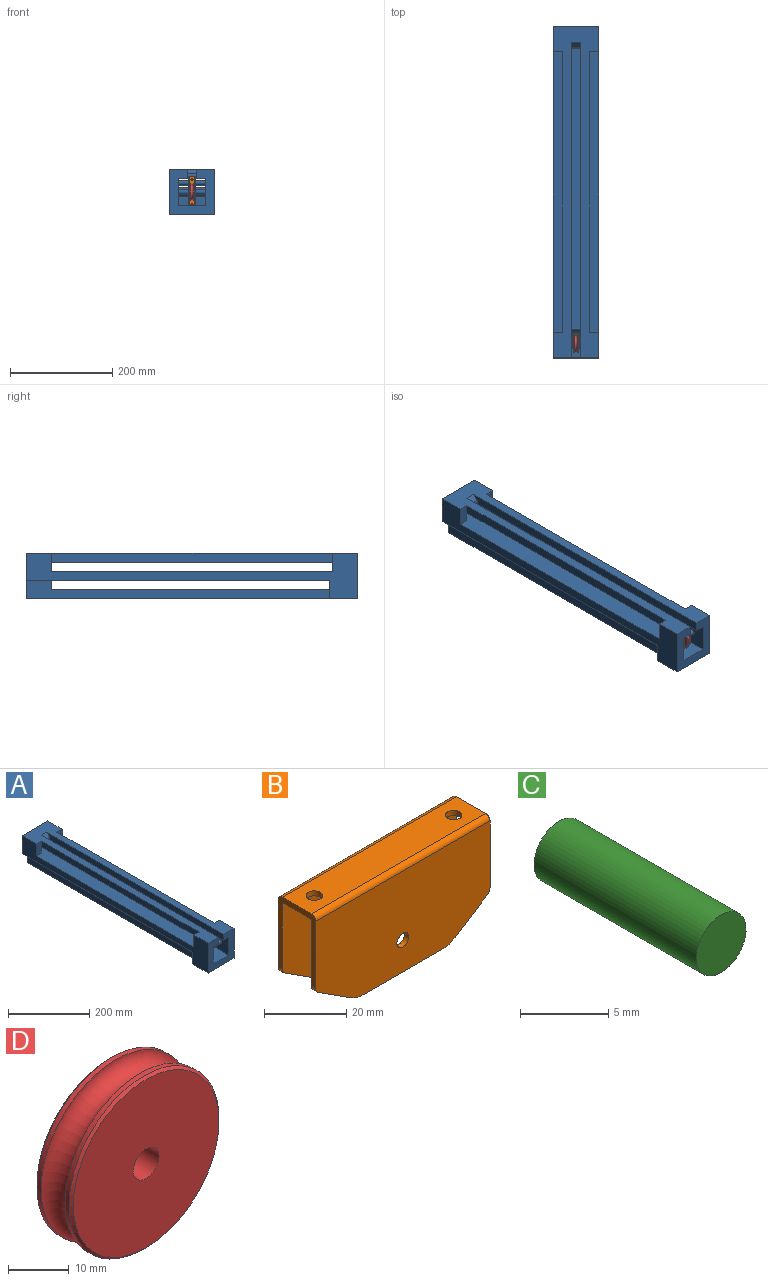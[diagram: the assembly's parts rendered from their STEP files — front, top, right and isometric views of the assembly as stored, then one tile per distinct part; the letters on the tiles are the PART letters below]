
ASSEMBLY  parts=4 mates=3
PART A: 35 faces, bbox 90x650x90 mm
  f0: plane 595x90mm, normal (0,0,-1), area 50850mm2, adj f7,f23,f28,f29,f30,f31,f32,f33
  f1: plane 36x18mm, normal (0,1,0), area 648mm2, adj f4,f9,f16,f22,f34
  f2: cylinder r=5mm len=54mm, axis (-1,0,0), area 1696.5mm2, adj f12,f16
  f3: cylinder r=5mm len=54mm, axis (-1,0,0), area 1696.5mm2, adj f10,f15
  f4: plane 650x90mm, normal (0,0,1), area 27576mm2, adj f1,f5,f7,f8,f9,f11,f13,f14
  f5: plane 90x90mm, normal (0,-1,0), area 4860mm2, adj f4,f6,f12,f16,f17,f18,f26,f27
  f6: plane 650x54mm, normal (0,0,-1), area 24120mm2, adj f5,f7,f8,f9,f10,f12,f15,f16
  f7: plane 90x90mm, normal (0,1,0), area 5832mm2, adj f0,f4,f6,f10,f15,f22,f27,f29
  f8: plane 550x18mm, normal (1,0,0), area 9900mm2, adj f4,f6,f11,f13
  f9: plane 550x18mm, normal (-1,0,0), area 9900mm2, adj f1,f4,f6,f14
  f10: plane 50x18mm, normal (-1,0,0), area 821.5mm2, adj f3,f6,f7,f11,f22
  f11: plane 36x18mm, normal (0,-1,0), area 648mm2, adj f4,f8,f10,f22,f33
  f12: plane 55x54mm, normal (-1,0,0), area 2736.5mm2, adj f2,f5,f6,f13,f21,f22,f23,f24
  f13: plane 36x18mm, normal (0,1,0), area 648mm2, adj f4,f8,f12,f22,f33
  f14: plane 36x18mm, normal (0,-1,0), area 648mm2, adj f4,f9,f15,f22,f34
  f15: plane 50x18mm, normal (1,0,0), area 821.5mm2, adj f3,f6,f7,f14,f22
  f16: plane 55x54mm, normal (1,0,0), area 2736.5mm2, adj f1,f2,f5,f6,f21,f22,f23,f24
  f17: plane 618x18mm, normal (1,0,0), area 10989.9mm2, adj f4,f5,f6,f19,f20,f25
  f18: plane 618x18mm, normal (-1,0,0), area 10989.9mm2, adj f4,f5,f6,f19,f20,f25
  f19: plane 18x9.75mm, normal (0,-0.71,0.71), area 248.1mm2, adj f4,f17,f18,f25
  f20: plane 18x0.61mm, normal (0,-0.48,-0.88), area 12.5mm2, adj f6,f17,f18,f25
  f21: plane 54x8mm, normal (0,-1,0), area 432mm2, adj f12,f16,f23,f24
  f22: plane 600x90mm, normal (0,0,1), area 51930mm2, adj f1,f7,f10,f11,f12,f13,f14,f15
  f23: plane 54x5mm, normal (0,-0.71,-0.71), area 381.8mm2, adj f0,f12,f16,f21
  f24: plane 54x5mm, normal (0,-0.71,0.71), area 381.8mm2, adj f12,f16,f21,f22
  f25: cylinder r=5mm len=18mm, axis (1,0,0), area 167mm2, adj f17,f18,f19,f20
  f26: plane 600x54mm, normal (0,0,1), area 32400mm2, adj f5,f12,f16,f28,f29,f30
  f27: plane 650x90mm, normal (0,0,-1), area 37080mm2, adj f5,f7,f29,f30,f31,f32,f33,f34
  f28: plane 54x18mm, normal (0,-1,0), area 972mm2, adj f0,f26,f29,f30
  f29: plane 595x36mm, normal (1,0,0), area 11610mm2, adj f0,f7,f26,f27,f28,f31
  f30: plane 595x36mm, normal (-1,0,0), area 11610mm2, adj f0,f7,f26,f27,f28,f32
  f31: plane 36x18mm, normal (0,1,0), area 648mm2, adj f0,f12,f27,f29,f33
  f32: plane 36x18mm, normal (0,1,0), area 648mm2, adj f0,f16,f27,f30,f34
  f33: plane 650x90mm, normal (1,0,0), area 17280mm2, adj f0,f4,f5,f7,f11,f13,f22,f27
  f34: plane 650x90mm, normal (-1,0,0), area 17280mm2, adj f0,f1,f4,f5,f7,f14,f22,f27
PART B: 30 faces, bbox 60x13x31.5 mm
  f0: cylinder r=2mm len=4mm, axis (0,0,1), area 18.8mm2, adj f2,f3
  f1: cylinder r=2mm len=4mm, axis (0,0,1), area 18.8mm2, adj f2,f3
  f2: plane 60x10mm, normal (0,0,1), area 574.9mm2, adj f0,f1,f4,f5,f6,f29
  f3: plane 60x9mm, normal (0,0,-1), area 514.9mm2, adj f0,f1,f5,f7,f9,f29
  f4: cylinder r=1.5mm len=60mm, axis (1,0,0), area 141.4mm2, adj f2,f5,f15,f29
  f5: plane 21.41x13mm, normal (-1,0,0), area 78.4mm2, adj f2,f3,f4,f6,f7,f8,f9,f12
  f6: cylinder r=1.5mm len=60mm, axis (1,0,0), area 141.4mm2, adj f2,f5,f28,f29
  f7: cylinder r=0.5mm len=60mm, axis (1,0,0), area 47.1mm2, adj f3,f5,f8,f29
  f8: plane 60x29.5mm, normal (0,-1,0), area 1629.4mm2, adj f5,f7,f13,f14,f18,f19,f22,f23
  f9: cylinder r=0.5mm len=60mm, axis (1,0,0), area 47.1mm2, adj f3,f5,f12,f29
  f10: cylinder r=8mm len=4.33mm, axis (0,-1,0), area 6.9mm2, adj f11,f12,f21,f28
  f11: plane 27.3x1.5mm, normal (0,0,-1), area 41mm2, adj f10,f12,f16,f28
  f12: plane 60x29.5mm, normal (0,1,0), area 1629.4mm2, adj f5,f9,f10,f11,f16,f17,f20,f21
  f13: cylinder r=8mm len=4.33mm, axis (0,-1,0), area 6.9mm2, adj f8,f14,f15,f23
  f14: plane 27.3x1.5mm, normal (0,0,-1), area 41mm2, adj f8,f13,f15,f18
  f15: plane 60x30mm, normal (0,1,0), area 1659.4mm2, adj f4,f5,f13,f14,f18,f19,f22,f23
  f16: cylinder r=8mm len=4.33mm, axis (0,1,0), area 6.9mm2, adj f11,f12,f17,f28
  f17: plane 11.11x7.14mm, normal (0.54,0,-0.84), area 19.8mm2, adj f12,f16,f24,f28
  f18: cylinder r=8mm len=4.33mm, axis (0,1,0), area 6.9mm2, adj f8,f14,f15,f19
  f19: plane 11.11x7.14mm, normal (0.54,0,-0.84), area 19.8mm2, adj f8,f15,f18,f25
  f20: cylinder r=2mm len=1.68mm, axis (0,1,0), area 3mm2, adj f5,f12,f21,f28
  f21: plane 11.11x7.14mm, normal (-0.54,0,-0.84), area 19.8mm2, adj f10,f12,f20,f28
  f22: cylinder r=2mm len=1.68mm, axis (0,1,0), area 3mm2, adj f5,f8,f15,f23
  f23: plane 11.11x7.14mm, normal (-0.54,0,-0.84), area 19.8mm2, adj f8,f13,f15,f22
  f24: cylinder r=2mm len=1.68mm, axis (0,-1,0), area 3mm2, adj f12,f17,f28,f29
  f25: cylinder r=2mm len=1.68mm, axis (0,-1,0), area 3mm2, adj f8,f15,f19,f29
  f26: cylinder r=2.05mm len=4.1mm, axis (0,-1,0), area 19.3mm2, adj f12,f28
  f27: cylinder r=2.05mm len=4.1mm, axis (0,-1,0), area 19.3mm2, adj f8,f15
  f28: plane 60x30mm, normal (0,-1,0), area 1659.4mm2, adj f5,f6,f10,f11,f16,f17,f20,f21
  f29: plane 21.41x13mm, normal (1,0,0), area 78.4mm2, adj f2,f3,f4,f6,f7,f8,f9,f12
PART C: 3 faces, bbox 4x13x4 mm
  f0: cylinder r=2mm len=13mm, axis (0,-1,0), area 163.4mm2, adj f1,f2
  f1: plane 4x4mm, normal (0,-1,0), area 12.6mm2, adj f0
  f2: plane 4x4mm, normal (0,1,0), area 12.6mm2, adj f0
PART D: 8 faces, bbox 42.2x8.5x42.2 mm
  f0: cone r=17mm half-angle=45deg, axis (0,1,0), area 76.6mm2, adj f1,f2
  f1: cylinder r=17.5mm len=35mm, axis (0,-1,0), area 104.5mm2, adj f0,f7
  f2: plane 34x34mm, normal (0,-1,0), area 879.6mm2, adj f0,f6
  f3: cone r=17mm half-angle=45deg, axis (0,-1,0), area 76.6mm2, adj f4,f5
  f4: cylinder r=17.5mm len=35mm, axis (0,-1,0), area 104.5mm2, adj f3,f7
  f5: plane 34x34mm, normal (0,1,0), area 879.6mm2, adj f3,f6
  f6: cylinder r=3mm len=8.5mm, axis (0,1,0), area 160.2mm2, adj f2,f5
  f7: torus R=17.5mm, axis (0,-1,0), area 868.7mm2, adj f1,f4
PLACE A t=(-45,325,-58)mm
PLACE B rot(axis=(-0.58,-0.58,-0.58),120deg) t=(-40.75,28,-45)mm
PLACE C rot(axis=(0,0,-1),90deg) t=(-40.75,28,-45)mm
PLACE D rot(axis=(0,0,-1),90deg) t=(-40.75,28,-45)mm
MATE revolute D.f0 <-> C.f0  axis (1,0,0) through (-45,28,-45)mm
MATE revolute B.f26 <-> C.f0  axis (-1,0,0) through (-51.5,28,-45)mm
MATE fastened B.f2 <-> A.f21  axis (0,1,0) through (-45,50,-45)mm
